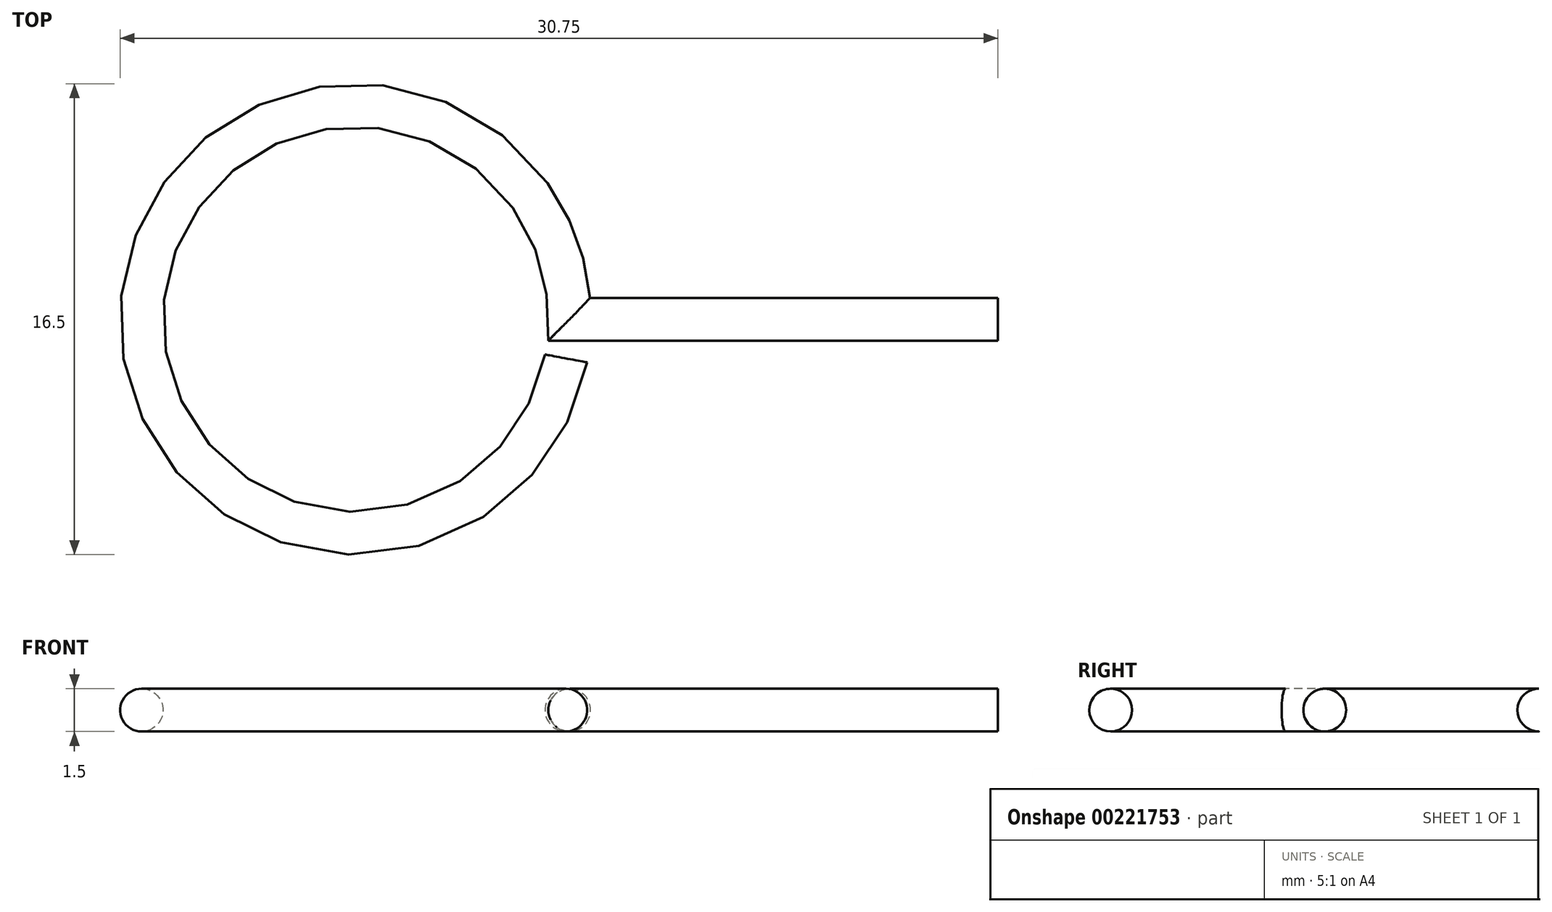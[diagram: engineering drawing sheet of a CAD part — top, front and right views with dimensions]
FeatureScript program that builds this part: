
annotation { "Feature Type Name" : "Feature", "Feature Type Description" : "" }
export const myFeature = defineFeature(function(context is Context, id is Id, definition is map)
    precondition{}
    {
        {
            var Q0;
            Q0=qCreatedBy(makeId("Top.planeOp"),FACE);
            var sketch = newSketch(context, id + "F0", { "sketchPlane" : qUnion([Q0])});
            skArc(sketch, "E0", {"start": v(7.5, 0) * mm, "mid": v(-7.47, 0.7) * mm, "end": v(7.37, -1.37) * mm});
            skLineSegment(sketch, "E1", {"start": v(7.5, 0) * mm, "end": v(22.5, 0) * mm});
            skSolve(sketch);
        }
        {
            var Q0;
            Q0=qCreatedBy(makeId("Right.planeOp"),FACE);
            cPlane(context, id + "F1", {"entities" : qUnion([Q0]), "cplaneType" : CPlaneType.OFFSET, "offset" : 22.5 * mm, "width" : 150 * mm, "height" : 150 * mm});
        }
        {
            var Q0;
            Q0=qCreatedBy(id+"F1.planeOp",FACE);
            var sketch = newSketch(context, id + "F2", { "sketchPlane" : qUnion([Q0])});
            skCircle(sketch, "E2", {"center": v(0, 0) * mm, "radius": 0.75 * mm});
            skSolve(sketch);
        }
        {
            var Q0;
            Q0 = qSketchRegion(id + "F2", true);
            var Q1;
            Q1 = qConstructionFilter(qBodyType(qCreatedBy(id + "F0" ,EDGE), BodyType.WIRE), ConstructionObject.NO);
            sweep(context, id + "F3", {"profiles" : qUnion([Q0]), "path" : qUnion([Q1])});
        }
    });
